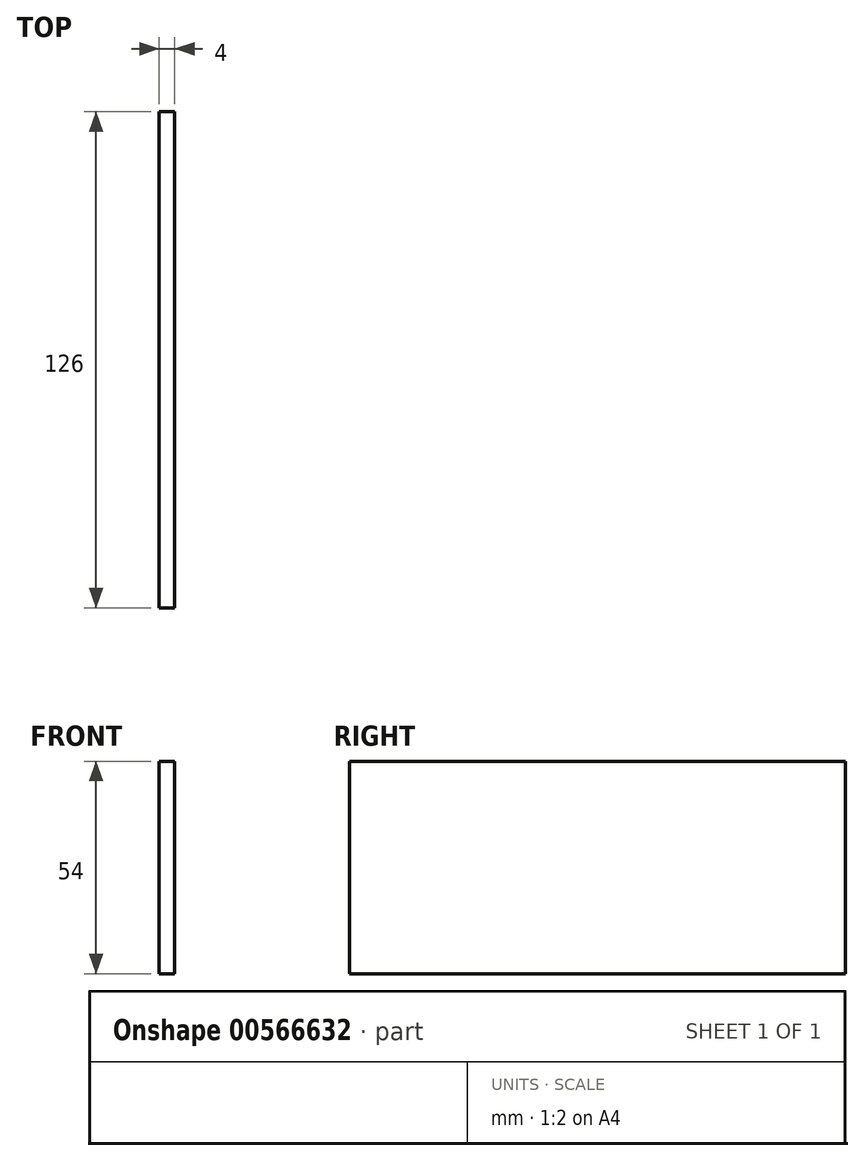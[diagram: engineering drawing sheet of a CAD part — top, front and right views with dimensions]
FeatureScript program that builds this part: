
annotation { "Feature Type Name" : "Feature", "Feature Type Description" : "" }
export const myFeature = defineFeature(function(context is Context, id is Id, definition is map)
    precondition{}
    {
        {
            var Q0;
            Q0=qCreatedBy(makeId("Right.planeOp"),FACE);
            var sketch = newSketch(context, id + "F0", { "sketchPlane" : qUnion([Q0])});
            skLineSegment(sketch, "E0.bottom", {"start": v(-63, 27) * mm, "end": v(63, 27) * mm});
            skLineSegment(sketch, "E0.top", {"start": v(-63, -27) * mm, "end": v(63, -27) * mm});
            skLineSegment(sketch, "E0.left", {"start": v(-63, 27) * mm, "end": v(-63, -27) * mm});
            skLineSegment(sketch, "E0.right", {"start": v(63, 27) * mm, "end": v(63, -27) * mm});
            skPoint(sketch, "E0.middle", {"position": v(0, 0) * mm});
            skSolve(sketch);
        }
        {
            var Q0;
            Q0=makeQuery(id+"F0.imprint","IMPRINT",FACE,{"disambiguationData":[TD([[makeQuery(id+"F0.imprint","IMPRINT",EDGE,{"derivedFrom":sQuery(id+"F0.wireOp",EDGE,"E0.bottom")}),-1.0]])]});
            extrude(context, id + "F1", {"entities" : qUnion([Q0]), "endBound" : BoundingType.SYMMETRIC, "depth" : 4 * mm, "offsetDistance" : 25 * mm});
        }
    });
